# Revit family: FOGLER LED
name_source: partatom
category: Lighting Fixtures
revit_build: Autodesk Revit Architecture 2015 (Build: 20140322_1515(x64)
units: mm (PartAtom-declared; Revit-internal decimal feet)

## types (1)
- KANLUX FOGLER LED 14W-NW 18121 LED 4000K 110° 800lm blacha stalowa biały
    Apparent Load = 14 VA
    Color Filter = 16777215
    Default Elevation = 0 mm  [stored 0 ft]
    Dimming Lamp Color Temperature Shift = <None>
    IP = IP20
    Klasyfikacja obciążenia = Oświetlenie
    Kod = 18121
    Kąt rozsyłu = 110°
    Lamp = LED
    Manufacturer = KANLUX
    Materiał klosz = KANLUX - klosz
    Materiał obudowa = KANLUX - obudowa - blacha stalowa, biały
    Moc oprawy = 14 W
    Model = FOGLER LED 14W-NW
    Photometric Web File = FOGLER LED 14W-NW.ies
    Tilt Angle = 90.00°
    URL = www.kanlux.pl
    Wattage Comments = 14
    Współczynnik mocy = 1
    Wysokość = 80 mm  [stored 0.262467 ft]
    Średnica = 290 mm  [stored 0.951444 ft]

note: [stored X ft] marks values corroborated as IEEE doubles in the binary element streams (Revit-internal decimal feet)
